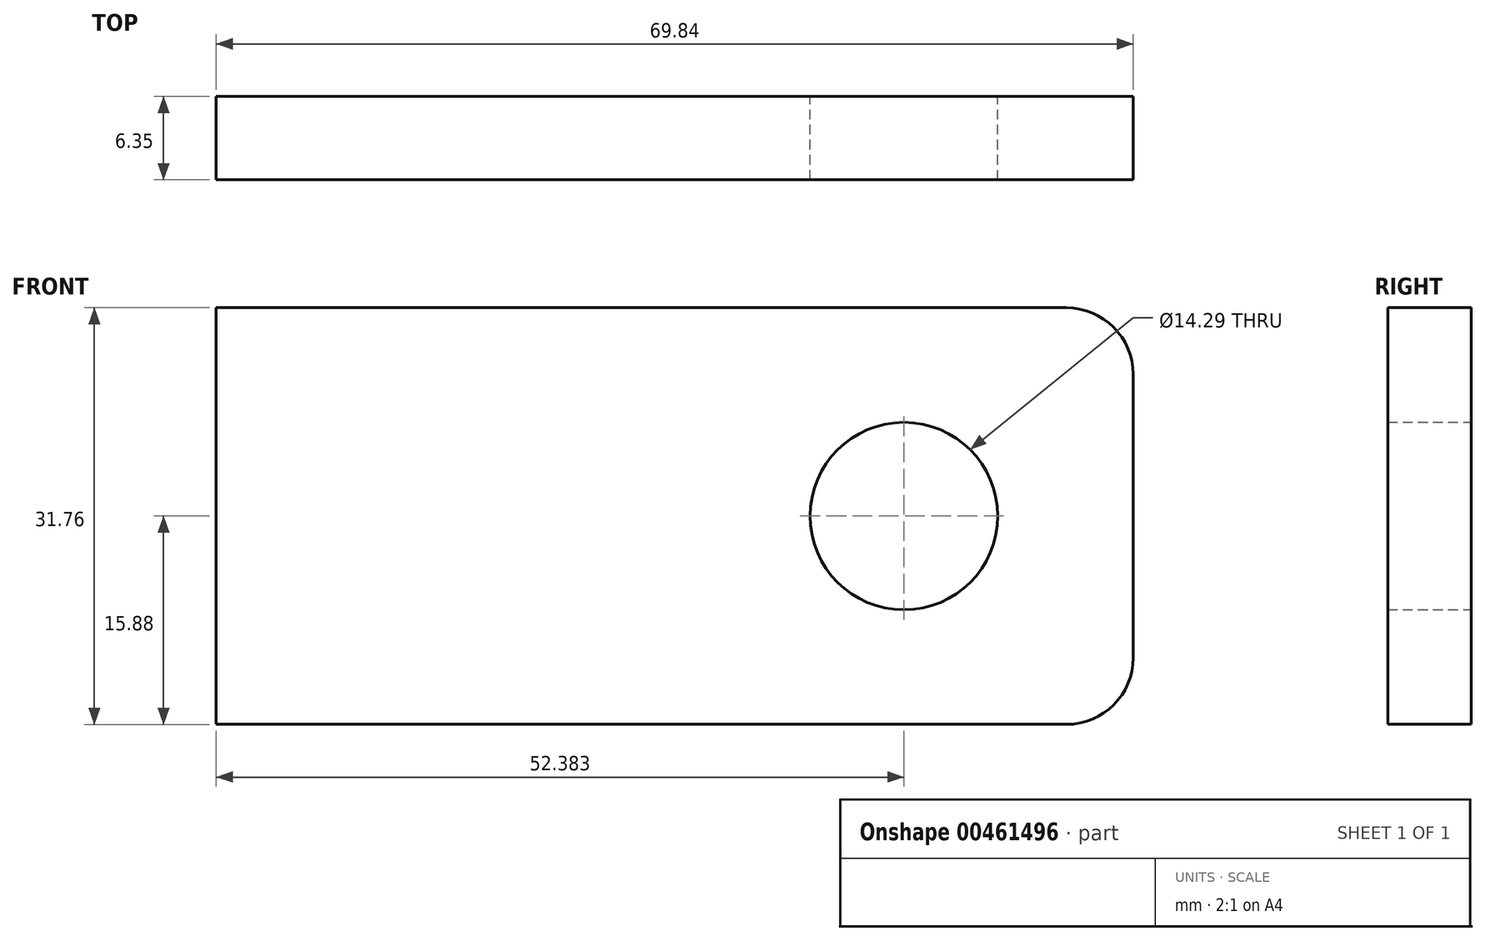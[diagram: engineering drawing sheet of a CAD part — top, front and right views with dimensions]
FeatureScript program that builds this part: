
annotation { "Feature Type Name" : "Feature", "Feature Type Description" : "" }
export const myFeature = defineFeature(function(context is Context, id is Id, definition is map)
    precondition{}
    {
        {
            var Q0;
            Q0=qCreatedBy(makeId("Front.planeOp"),FACE);
            var sketch = newSketch(context, id + "F0", { "sketchPlane" : qUnion([Q0])});
            skLineSegment(sketch, "E0.bottom", {"start": v(34.93, -15.87) * mm, "end": v(-34.93, -15.88) * mm});
            skLineSegment(sketch, "E0.top", {"start": v(34.93, 15.88) * mm, "end": v(-34.93, 15.87) * mm});
            skLineSegment(sketch, "E0.left", {"start": v(34.93, -15.87) * mm, "end": v(34.93, 15.88) * mm});
            skLineSegment(sketch, "E0.right", {"start": v(-34.93, -15.88) * mm, "end": v(-34.93, 15.87) * mm});
            skPoint(sketch, "E0.middle", {"position": v(0, 0) * mm});
            skCircle(sketch, "E1", {"center": v(17.46, 0) * mm, "radius": 7.14 * mm});
            skPoint(sketch, "E1.centerSnap0", {"position": v(-34.93, 0) * mm});
            skSolve(sketch);
        }
        {
            var Q0;
            Q0 = qSketchRegion(id + "F0", true);
            extrude(context, id + "F1", {"entities" : qUnion([Q0]), "depth" : 6.35 * mm});
        }
        {
            var Q0;
            Q0=makeQuery(id+"F1.opExtrude","SWEPT_EDGE",EDGE,{"disambiguationData":[OSD([sQuery(id+"F0.wireOp",EDGE,"E0.top"),sQuery(id+"F0.wireOp",EDGE,"E0.left")])]});
            var Q1;
            Q1=makeQuery(id+"F1.opExtrude","SWEPT_EDGE",EDGE,{"disambiguationData":[OSD([sQuery(id+"F0.wireOp",EDGE,"E0.bottom"),sQuery(id+"F0.wireOp",EDGE,"E0.left")])]});
            fillet(context, id + "F2", {"entities" : qUnion([Q0, Q1]), "radius" : 5.08 * mm, "tangentPropagation" : true, "allowEdgeOverflow" : false});
        }
    });
